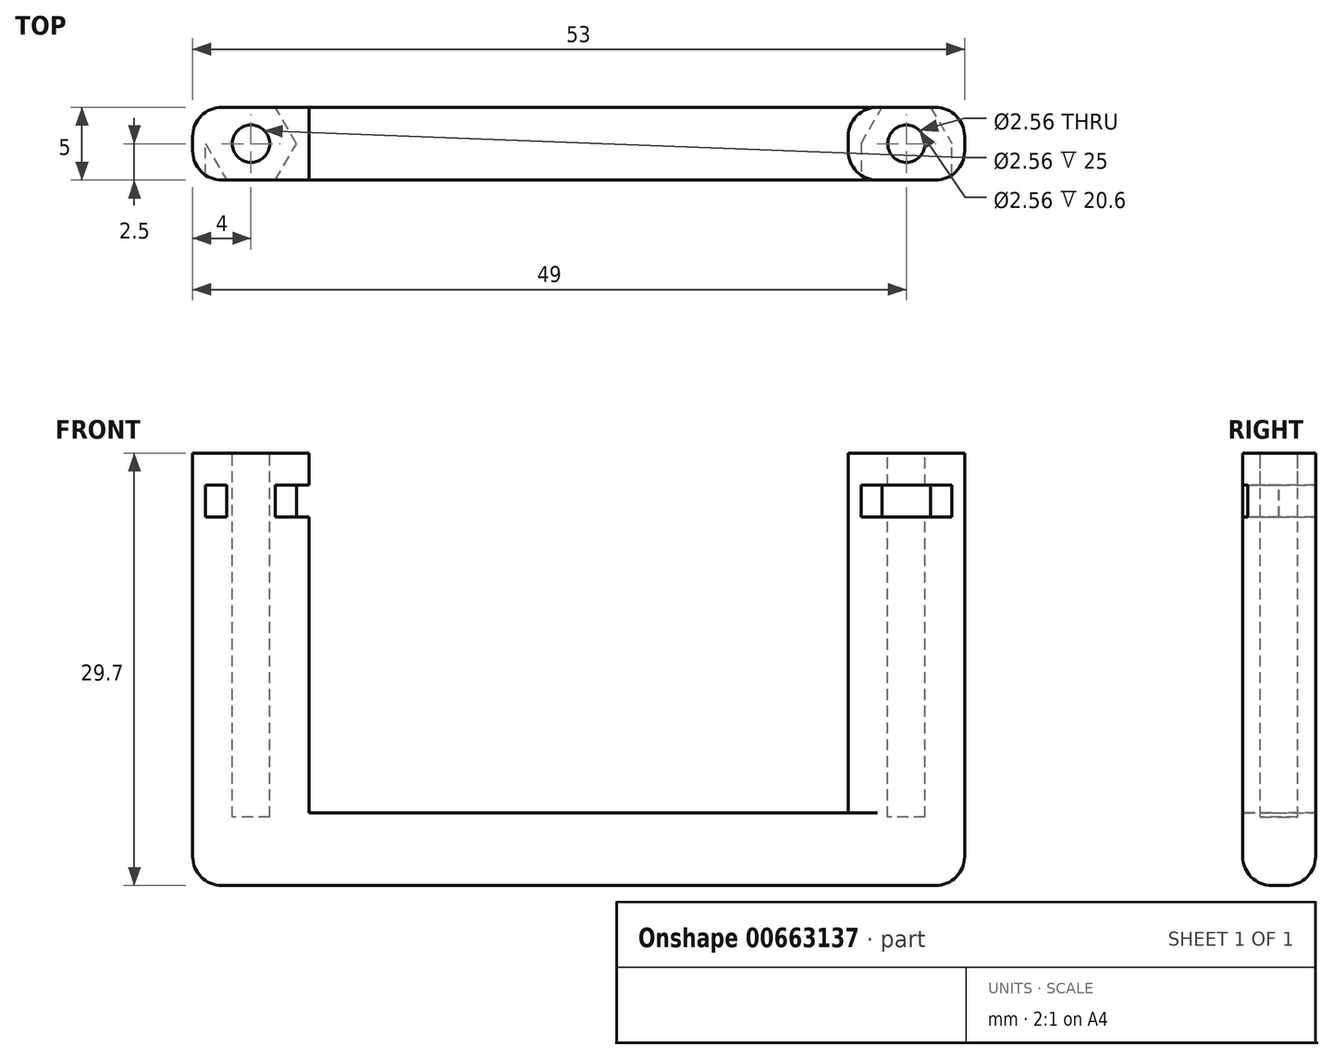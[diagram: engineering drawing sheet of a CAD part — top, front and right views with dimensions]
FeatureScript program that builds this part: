
annotation { "Feature Type Name" : "Feature", "Feature Type Description" : "" }
export const myFeature = defineFeature(function(context is Context, id is Id, definition is map)
    precondition{}
    {
        {
            var Q0;
            Q0=qCreatedBy(makeId("Front.planeOp"),FACE);
            var sketch = newSketch(context, id + "F0", { "sketchPlane" : qUnion([Q0])});
            skLineSegment(sketch, "E0", {"start": v(0, 0) * mm, "end": v(22.5, 0) * mm});
            skLineSegment(sketch, "E1", {"start": v(22.5, 0) * mm, "end": v(22.5, 22.5) * mm, "construction": true});
            skLineSegment(sketch, "E2", {"start": v(22.5, 0) * mm, "end": v(18.5, 0) * mm});
            skLineSegment(sketch, "E3", {"start": v(18.5, 0) * mm, "end": v(18.5, 22.5) * mm});
            skLineSegment(sketch, "E4", {"start": v(18.5, 22.5) * mm, "end": v(26.5, 22.5) * mm});
            skLineSegment(sketch, "E5", {"start": v(26.5, 22.5) * mm, "end": v(26.5, 0) * mm});
            skLineSegment(sketch, "E6", {"start": v(26.5, 0) * mm, "end": v(18.5, 0) * mm});
            skLineSegment(sketch, "E7", {"start": v(26.5, 0) * mm, "end": v(26.5, -5) * mm});
            skLineSegment(sketch, "E8", {"start": v(26.5, -5) * mm, "end": v(0, -5) * mm});
            skLineSegment(sketch, "E9", {"start": v(0, -5) * mm, "end": v(0, 0) * mm});
            skLineSegment(sketch, "E10", {"start": v(22.5, 24) * mm, "end": v(22.5, 22.5) * mm, "construction": true});
            skLineSegment(sketch, "E11", {"start": v(22.5, 22.5) * mm, "end": v(22.5, 20.5) * mm, "construction": true});
            skLineSegment(sketch, "E12", {"start": v(22.5, 20.5) * mm, "end": v(25.1, 20.5) * mm, "construction": true});
            skLineSegment(sketch, "E13", {"start": v(25.1, 20.5) * mm, "end": v(19.9, 20.5) * mm});
            skLineSegment(sketch, "E14", {"start": v(19.9, 20.5) * mm, "end": v(19.9, 22.5) * mm});
            skLineSegment(sketch, "E15", {"start": v(19.9, 22.5) * mm, "end": v(25.1, 22.5) * mm});
            skLineSegment(sketch, "E16", {"start": v(25.1, 22.5) * mm, "end": v(25.1, 20.5) * mm});
            skLineSegment(sketch, "E17", {"start": v(0, -11.25) * mm, "end": v(0, 30.63) * mm, "construction": true});
            skLineSegment(sketch, "E18.MirrorCS", {"start": v(-22.5, 24) * mm, "end": v(-22.5, 22.5) * mm, "construction": true});
            skLineSegment(sketch, "E19.MirrorCS", {"start": v(-22.5, 22.5) * mm, "end": v(-22.5, 20.5) * mm, "construction": true});
            skLineSegment(sketch, "E20.MirrorCS", {"start": v(-22.5, 0) * mm, "end": v(-18.5, 0) * mm});
            skLineSegment(sketch, "E21.MirrorCS", {"start": v(-19.9, 22.5) * mm, "end": v(-25.1, 22.5) * mm});
            skLineSegment(sketch, "E22.MirrorCS", {"start": v(-22.5, 0) * mm, "end": v(-22.5, 22.5) * mm, "construction": true});
            skLineSegment(sketch, "E23.MirrorCS", {"start": v(-22.5, 20.5) * mm, "end": v(-25.1, 20.5) * mm, "construction": true});
            skLineSegment(sketch, "E24.MirrorCS", {"start": v(-26.5, -5) * mm, "end": v(0, -5) * mm});
            skLineSegment(sketch, "E25.MirrorCS", {"start": v(-26.5, 0) * mm, "end": v(-26.5, -5) * mm});
            skLineSegment(sketch, "E26.MirrorCS", {"start": v(0, 0) * mm, "end": v(-22.5, 0) * mm});
            skLineSegment(sketch, "E27.MirrorCS", {"start": v(-18.5, 0) * mm, "end": v(-18.5, 22.5) * mm});
            skLineSegment(sketch, "E28.MirrorCS", {"start": v(-18.5, 22.5) * mm, "end": v(-26.5, 22.5) * mm});
            skLineSegment(sketch, "E29.MirrorCS", {"start": v(-26.5, 22.5) * mm, "end": v(-26.5, 0) * mm});
            skLineSegment(sketch, "E30.MirrorCS", {"start": v(-26.5, 0) * mm, "end": v(-18.5, 0) * mm});
            skLineSegment(sketch, "E31.MirrorCS", {"start": v(-19.9, 20.5) * mm, "end": v(-19.9, 22.5) * mm});
            skLineSegment(sketch, "E32.MirrorCS", {"start": v(-25.1, 22.5) * mm, "end": v(-25.1, 20.5) * mm});
            skLineSegment(sketch, "E33.MirrorCS", {"start": v(-25.1, 20.5) * mm, "end": v(-19.9, 20.5) * mm});
            skSolve(sketch);
        }
        {
            var Q0;
            {var subQ2=sQuery(id+"F0.wireOp",EDGE,"E0");Q0=makeQuery(id+"F0.imprint","IMPRINT",FACE,{"disambiguationData":[TD([[makeQuery(id+"F0.imprint","IMPRINT",EDGE,{"derivedFrom":subQ2}),-1.0]])]});}
            var Q1;
            {var subQ4=sQuery(id+"F0.wireOp",EDGE,"E3");Q1=makeQuery(id+"F0.imprint","IMPRINT",FACE,{"disambiguationData":[TD([[makeQuery(id+"F0.imprint","IMPRINT",EDGE,{"derivedFrom":subQ4}),-1.0]])]});}
            var Q2;
            Q2=makeQuery(id+"F0.imprint","IMPRINT",FACE,{"disambiguationData":[TD([[makeQuery(id+"F0.imprint","IMPRINT",EDGE,{"derivedFrom":sQuery(id+"F0.wireOp",EDGE,"E13")}),-1.0]])]});
            var Q3;
            Q3=makeQuery(id+"F0.imprint","IMPRINT",FACE,{"disambiguationData":[TD([[makeQuery(id+"F0.imprint","IMPRINT",EDGE,{"derivedFrom":sQuery(id+"F0.wireOp",EDGE,"E9")}),1.0]])]});
            var Q4;
            {var subQ3=sQuery(id+"F0.wireOp",EDGE,"E27.MirrorCS");Q4=makeQuery(id+"F0.imprint","IMPRINT",FACE,{"disambiguationData":[TD([[makeQuery(id+"F0.imprint","IMPRINT",EDGE,{"derivedFrom":subQ3}),1.0]])]});}
            var Q5;
            {var subQ0=sQuery(id+"F0.wireOp",EDGE,"E31.MirrorCS");Q5=makeQuery(id+"F0.imprint","IMPRINT",FACE,{"disambiguationData":[TD([[makeQuery(id+"F0.imprint","IMPRINT",EDGE,{"derivedFrom":subQ0}),1.0]])]});}
            extrude(context, id + "F1", {"entities" : qUnion([Q0, Q1, Q2, Q3, Q4, Q5]), "endBound" : BoundingType.SYMMETRIC, "depth" : 5 * mm, "offsetDistance" : 25 * mm});
        }
        {
            var Q0;
            {var subQ0=sQuery(id+"F0.wireOp",EDGE,"E4");Q0=makeQuery(id+"F1.opExtrude","SWEPT_FACE",FACE,{"disambiguationData":[OSD([subQ0]),TDD([makeQuery(id+"F0.imprint","IMPRINT",EDGE,{"disambiguationData":[TD([[makeQuery(id+"F0.imprint","INTERSECT",VERTEX,{"derivedFrom":[subQ0,sQuery(id+"F0.wireOp",EDGE,"E5")]}),1.0]])],"derivedFrom":subQ0})])]});}
            var sketch = newSketch(context, id + "F2", { "sketchPlane" : qUnion([Q0])});
            skPoint(sketch, "E34", {"position": v(18.5, 2.5) * mm});
            skPoint(sketch, "E35", {"position": v(18.5, -2.5) * mm});
            skLineSegment(sketch, "E36", {"start": v(26.5, -2.5) * mm, "end": v(18.5, -2.5) * mm});
            skLineSegment(sketch, "E37", {"start": v(18.5, 2.5) * mm, "end": v(26.5, 2.5) * mm});
            skLineSegment(sketch, "E38", {"start": v(26.5, 2.5) * mm, "end": v(26.5, -2.5) * mm});
            skLineSegment(sketch, "E39", {"start": v(18.5, -2.5) * mm, "end": v(18.5, 2.5) * mm});
            skLineSegment(sketch, "E40", {"start": v(18.5, 2.5) * mm, "end": v(22.5, 2.5) * mm, "construction": true});
            skLineSegment(sketch, "E41", {"start": v(22.5, 2.5) * mm, "end": v(22.5, 0) * mm, "construction": true});
            skCircle(sketch, "E42.cCircle", {"center": v(22.5, 0) * mm, "radius": 2.7 * mm, "construction": true});
            skLineSegment(sketch, "E42.0", {"start": v(24.05, 2.7) * mm, "end": v(25.62, 0.01) * mm});
            skLineSegment(sketch, "E42.1", {"start": v(25.62, 0.01) * mm, "end": v(24.07, -2.7) * mm});
            skLineSegment(sketch, "E42.2", {"start": v(24.07, -2.7) * mm, "end": v(20.95, -2.7) * mm});
            skLineSegment(sketch, "E42.3", {"start": v(20.95, -2.7) * mm, "end": v(19.38, -0.01) * mm});
            skLineSegment(sketch, "E42.4", {"start": v(19.38, -0.01) * mm, "end": v(20.93, 2.7) * mm});
            skLineSegment(sketch, "E42.5", {"start": v(20.93, 2.7) * mm, "end": v(24.05, 2.7) * mm});
            skPoint(sketch, "E42.0.midPoint", {"position": v(24.83, 1.36) * mm});
            skLineSegment(sketch, "E43", {"start": v(19.38, -0.01) * mm, "end": v(19.38, -2.5) * mm});
            skLineSegment(sketch, "E44", {"start": v(19.38, -2.5) * mm, "end": v(25.62, -2.5) * mm});
            skLineSegment(sketch, "E45", {"start": v(25.62, -2.5) * mm, "end": v(25.62, 0.01) * mm});
            skLineSegment(sketch, "E46.MirrorCS", {"start": v(-19.38, -2.5) * mm, "end": v(-25.62, -2.5) * mm});
            skLineSegment(sketch, "E47.MirrorCS", {"start": v(-20.95, -2.7) * mm, "end": v(-19.38, -0.01) * mm});
            skLineSegment(sketch, "E48.MirrorCS", {"start": v(-20.93, 2.7) * mm, "end": v(-24.05, 2.7) * mm});
            skLineSegment(sketch, "E49.MirrorCS", {"start": v(-24.07, -2.7) * mm, "end": v(-20.95, -2.7) * mm});
            skLineSegment(sketch, "E50.MirrorCS", {"start": v(-25.62, 0.01) * mm, "end": v(-24.07, -2.7) * mm});
            skLineSegment(sketch, "E51.MirrorCS", {"start": v(-24.05, 2.7) * mm, "end": v(-25.62, 0.01) * mm});
            skPoint(sketch, "E52.MirrorP", {"position": v(-18.5, -2.5) * mm});
            skLineSegment(sketch, "E53.MirrorCS", {"start": v(-18.5, 2.5) * mm, "end": v(-22.5, 2.5) * mm, "construction": true});
            skLineSegment(sketch, "E54.MirrorCS", {"start": v(-22.5, 2.5) * mm, "end": v(-22.5, 0) * mm, "construction": true});
            skPoint(sketch, "E55.MirrorP", {"position": v(-18.5, 2.5) * mm});
            skPoint(sketch, "E56.MirrorP", {"position": v(-24.83, 1.36) * mm});
            skLineSegment(sketch, "E57.MirrorCS", {"start": v(-19.38, -0.01) * mm, "end": v(-19.38, -2.5) * mm});
            skLineSegment(sketch, "E58.MirrorCS", {"start": v(-19.38, -0.01) * mm, "end": v(-20.93, 2.7) * mm});
            skLineSegment(sketch, "E59.MirrorCS", {"start": v(-18.5, -2.5) * mm, "end": v(-18.5, 2.5) * mm});
            skLineSegment(sketch, "E60.MirrorCS", {"start": v(-25.62, -2.5) * mm, "end": v(-25.62, 0.01) * mm});
            skLineSegment(sketch, "E61.MirrorCS", {"start": v(-26.5, -2.5) * mm, "end": v(-18.5, -2.5) * mm});
            skCircle(sketch, "E62.MirrorC", {"center": v(-22.5, 0) * mm, "radius": 2.7 * mm, "construction": true});
            skLineSegment(sketch, "E63.MirrorCS", {"start": v(-18.5, 2.5) * mm, "end": v(-26.5, 2.5) * mm});
            skLineSegment(sketch, "E64.MirrorCS", {"start": v(-26.5, 2.5) * mm, "end": v(-26.5, -2.5) * mm});
            skSolve(sketch);
        }
        {
            var Q0;
            {var subQ0=sQuery(id+"F2.wireOp",EDGE,"E43");Q0=makeQuery(id+"F2.imprint","IMPRINT",FACE,{"disambiguationData":[TD([[makeQuery(id+"F2.imprint","IMPRINT",EDGE,{"derivedFrom":subQ0}),1.0]])]});}
            var Q1;
            {var subQ1=sQuery(id+"F2.wireOp",EDGE,"E42.1");Q1=makeQuery(id+"F2.imprint","IMPRINT",FACE,{"disambiguationData":[TD([[makeQuery(id+"F2.imprint","IMPRINT",EDGE,{"derivedFrom":subQ1}),-1.0]])]});}
            var Q2;
            {var subQ0=sQuery(id+"F2.wireOp",EDGE,"E42.1");Q2=makeQuery(id+"F2.imprint","IMPRINT",FACE,{"disambiguationData":[TD([[makeQuery(id+"F2.imprint","IMPRINT",EDGE,{"derivedFrom":subQ0}),1.0]])]});}
            var Q3;
            {var subQ0=sQuery(id+"F2.wireOp",EDGE,"E50.MirrorCS");Q3=makeQuery(id+"F2.imprint","IMPRINT",FACE,{"disambiguationData":[TD([[makeQuery(id+"F2.imprint","IMPRINT",EDGE,{"derivedFrom":subQ0}),1.0]])]});}
            var Q4;
            {var subQ0=sQuery(id+"F2.wireOp",EDGE,"E50.MirrorCS");Q4=makeQuery(id+"F2.imprint","IMPRINT",FACE,{"disambiguationData":[TD([[makeQuery(id+"F2.imprint","IMPRINT",EDGE,{"derivedFrom":subQ0}),-1.0]])]});}
            var Q5;
            {var subQ0=sQuery(id+"F2.wireOp",EDGE,"E57.MirrorCS");Q5=makeQuery(id+"F2.imprint","IMPRINT",FACE,{"disambiguationData":[TD([[makeQuery(id+"F2.imprint","IMPRINT",EDGE,{"derivedFrom":subQ0}),-1.0]])]});}
            var Q6;
            {var subQ6=sQuery(id+"F2.wireOp",EDGE,"E47.MirrorCS");var subQ9=sQuery(id+"F2.wireOp",EDGE,"E61.MirrorCS");var subQ11=makeQuery(id+"F2.imprint","INTERSECT",VERTEX,{"derivedFrom":[subQ6,subQ9]});Q6=makeQuery(id+"F2.imprint","IMPRINT",FACE,{"disambiguationData":[TD([[makeQuery(id+"F2.imprint","IMPRINT",EDGE,{"disambiguationData":[TD([[subQ11,1.0]])],"derivedFrom":subQ9}),1.0]])]});}
            var Q7;
            {var subQ5=sQuery(id+"F2.wireOp",EDGE,"E42.4");var subQ9=sQuery(id+"F2.wireOp",EDGE,"E37");var subQ11=makeQuery(id+"F2.imprint","INTERSECT",VERTEX,{"derivedFrom":[subQ9,subQ5]});Q7=makeQuery(id+"F2.imprint","IMPRINT",FACE,{"disambiguationData":[TD([[makeQuery(id+"F2.imprint","IMPRINT",EDGE,{"disambiguationData":[TD([[subQ11,-1.0]])],"derivedFrom":subQ9}),-1.0]])]});}
            extrude(context, id + "F3", {"entities" : qUnion([Q0, Q1, Q2, Q3, Q4, Q5, Q6, Q7]), "operationType" : NewBodyOperationType.REMOVE, "oppositeDirection" : true, "depth" : 2.2 * mm, "offsetDistance" : 25 * mm});
        }
        {
            var Q0;
            {var subQ6=sQuery(id+"F0.wireOp",EDGE,"E15");var subQ10=sQuery(id+"F0.wireOp",EDGE,"E4");Q0=makeQuery(id+"F3.boolean.opBoolean","SPLIT",FACE,{"disambiguationData":[TD([makeQuery(id+"F3.opExtrude","SWEPT_FACE",FACE,{"disambiguationData":[OSD([sQuery(id+"F2.wireOp",EDGE,"E42.0")])]})])],"derivedFrom":makeQuery(id+"F1.opExtrude","SWEPT_FACE",FACE,{"disambiguationData":[OSD([subQ10,subQ6])]})});}
            var sketch = newSketch(context, id + "F4", { "sketchPlane" : qUnion([Q0])});
            skLineSegment(sketch, "E65", {"start": v(-26.5, 2.5) * mm, "end": v(-18.5, 2.5) * mm});
            skLineSegment(sketch, "E66", {"start": v(-18.5, 2.5) * mm, "end": v(-18.5, -2.5) * mm});
            skLineSegment(sketch, "E67", {"start": v(-18.5, -2.5) * mm, "end": v(-26.5, -2.5) * mm});
            skLineSegment(sketch, "E68", {"start": v(-26.5, -2.5) * mm, "end": v(-26.5, 2.5) * mm});
            skPoint(sketch, "E69", {"position": v(18.5, 2.5) * mm});
            skPoint(sketch, "E70", {"position": v(18.5, -2.5) * mm});
            skLineSegment(sketch, "E71", {"start": v(26.5, 2.5) * mm, "end": v(18.5, 2.5) * mm});
            skLineSegment(sketch, "E72", {"start": v(18.5, -2.5) * mm, "end": v(26.5, -2.5) * mm});
            skLineSegment(sketch, "E73", {"start": v(26.5, -2.5) * mm, "end": v(26.5, 2.5) * mm});
            skLineSegment(sketch, "E74", {"start": v(18.5, -2.5) * mm, "end": v(18.5, 2.5) * mm});
            skSolve(sketch);
        }
        {
            var Q0;
            Q0=makeQuery(id+"F4.imprint","IMPRINT",FACE,{"disambiguationData":[TD([[makeQuery(id+"F4.imprint","IMPRINT",EDGE,{"derivedFrom":sQuery(id+"F4.wireOp",EDGE,"E65")}),-1.0]])]});
            var Q1;
            {var subQ3=sQuery(id+"F4.wireOp",EDGE,"E74");Q1=makeQuery(id+"F4.imprint","IMPRINT",FACE,{"disambiguationData":[TD([[makeQuery(id+"F4.imprint","IMPRINT",EDGE,{"derivedFrom":subQ3}),-1.0]])]});}
            var Q2;
            {var subQ0=sQuery(id+"F4.wireOp",EDGE,"E73");Q2=makeQuery(id+"F4.imprint","IMPRINT",FACE,{"disambiguationData":[TD([[makeQuery(id+"F4.imprint","IMPRINT",EDGE,{"derivedFrom":subQ0}),1.0]])]});}
            extrude(context, id + "F5", {"entities" : qUnion([Q0, Q1, Q2]), "operationType" : NewBodyOperationType.ADD, "depth" : 2.2 * mm, "offsetDistance" : 25 * mm});
        }
        {
            var Q0;
            Q0=makeQuery(id+"F5.opExtrude","CAP_FACE",FACE,{"disambiguationData":[OSD([sQuery(id+"F4.wireOp",EDGE,"E71"),sQuery(id+"F4.wireOp",EDGE,"E72"),sQuery(id+"F4.wireOp",EDGE,"E73"),sQuery(id+"F4.wireOp",EDGE,"E74")])],"isStart":false});
            var sketch = newSketch(context, id + "F6", { "sketchPlane" : qUnion([Q0])});
            skLineSegment(sketch, "E75", {"start": v(-26.5, 2.5) * mm, "end": v(-22.5, 2.5) * mm, "construction": true});
            skLineSegment(sketch, "E76", {"start": v(-22.5, 2.5) * mm, "end": v(-22.5, 0) * mm, "construction": true});
            skLineSegment(sketch, "E77", {"start": v(18.5, 2.5) * mm, "end": v(22.5, 2.5) * mm, "construction": true});
            skLineSegment(sketch, "E78", {"start": v(22.5, 2.5) * mm, "end": v(22.5, 0) * mm, "construction": true});
            skCircle(sketch, "E79", {"center": v(22.5, 0) * mm, "radius": 1.28 * mm});
            skCircle(sketch, "E80", {"center": v(-22.5, 0) * mm, "radius": 1.28 * mm});
            skSolve(sketch);
        }
        {
            var Q0;
            Q0=makeQuery(id+"F6.imprint","IMPRINT",FACE,{"disambiguationData":[TD([[makeQuery(id+"F6.imprint","IMPRINT",EDGE,{"derivedFrom":sQuery(id+"F6.wireOp",EDGE,"E80")}),1.0]])]});
            var Q1;
            Q1=makeQuery(id+"F6.imprint","IMPRINT",FACE,{"disambiguationData":[TD([[makeQuery(id+"F6.imprint","IMPRINT",EDGE,{"derivedFrom":sQuery(id+"F6.wireOp",EDGE,"E79")}),1.0]])]});
            extrude(context, id + "F7", {"entities" : qUnion([Q0, Q1]), "operationType" : NewBodyOperationType.REMOVE, "oppositeDirection" : true, "depth" : 25 * mm, "offsetDistance" : 25 * mm});
        }
        {
            var Q0;
            Q0=makeQuery(id+"F1.opExtrude","SWEPT_FACE",FACE,{"disambiguationData":[OSD([sQuery(id+"F0.wireOp",EDGE,"E8"),sQuery(id+"F0.wireOp",EDGE,"E24.MirrorCS")])]});
            var Q1;
            Q1=makeQuery(id+"F5.boolean.opBoolean","MERGE",EDGE,{"derivedFrom":[makeQuery(id+"F1.opExtrude","CAP_EDGE",EDGE,{"disambiguationData":[OSD([sQuery(id+"F0.wireOp",EDGE,"E3")])],"isStart":false}),makeQuery(id+"F5.opExtrude","SWEPT_EDGE",EDGE,{"disambiguationData":[OSD([sQuery(id+"F4.wireOp",EDGE,"E72"),sQuery(id+"F4.wireOp",EDGE,"E74")])]})]});
            var Q2;
            Q2=makeQuery(id+"F5.boolean.opBoolean","MERGE",EDGE,{"derivedFrom":[makeQuery(id+"F1.opExtrude","CAP_EDGE",EDGE,{"disambiguationData":[OSD([sQuery(id+"F0.wireOp",EDGE,"E3")])],"isStart":true}),makeQuery(id+"F5.opExtrude","SWEPT_EDGE",EDGE,{"disambiguationData":[OSD([sQuery(id+"F4.wireOp",EDGE,"E71"),sQuery(id+"F4.wireOp",EDGE,"E74")])]})]});
            var Q3;
            Q3=makeQuery(id+"F5.boolean.opBoolean","MERGE",EDGE,{"derivedFrom":[makeQuery(id+"F1.opExtrude","CAP_EDGE",EDGE,{"disambiguationData":[OSD([sQuery(id+"F0.wireOp",EDGE,"E5"),sQuery(id+"F0.wireOp",EDGE,"E7")])],"isStart":false}),makeQuery(id+"F5.opExtrude","SWEPT_EDGE",EDGE,{"disambiguationData":[OSD([sQuery(id+"F4.wireOp",EDGE,"E72"),sQuery(id+"F4.wireOp",EDGE,"E73")])]})]});
            var Q4;
            Q4=makeQuery(id+"F1.opExtrude","CAP_EDGE",EDGE,{"disambiguationData":[OSD([sQuery(id+"F0.wireOp",EDGE,"E5"),sQuery(id+"F0.wireOp",EDGE,"E7")])],"isStart":true});
            var Q5;
            Q5=makeQuery(id+"F5.boolean.opBoolean","MERGE",EDGE,{"derivedFrom":[makeQuery(id+"F1.opExtrude","CAP_EDGE",EDGE,{"disambiguationData":[OSD([sQuery(id+"F0.wireOp",EDGE,"E25.MirrorCS"),sQuery(id+"F0.wireOp",EDGE,"E29.MirrorCS")])],"isStart":false}),makeQuery(id+"F5.opExtrude","SWEPT_EDGE",EDGE,{"disambiguationData":[OSD([sQuery(id+"F4.wireOp",EDGE,"E67"),sQuery(id+"F4.wireOp",EDGE,"E68")])]})]});
            var Q6;
            Q6=makeQuery(id+"F5.boolean.opBoolean","MERGE",EDGE,{"derivedFrom":[makeQuery(id+"F1.opExtrude","CAP_EDGE",EDGE,{"disambiguationData":[OSD([sQuery(id+"F0.wireOp",EDGE,"E25.MirrorCS"),sQuery(id+"F0.wireOp",EDGE,"E29.MirrorCS")])],"isStart":true}),makeQuery(id+"F5.opExtrude","SWEPT_EDGE",EDGE,{"disambiguationData":[OSD([sQuery(id+"F4.wireOp",EDGE,"E65"),sQuery(id+"F4.wireOp",EDGE,"E68")])]})]});
            var Q7;
            Q7=makeQuery(id+"F5.boolean.opBoolean","MERGE",EDGE,{"derivedFrom":[makeQuery(id+"F1.opExtrude","CAP_EDGE",EDGE,{"disambiguationData":[OSD([sQuery(id+"F0.wireOp",EDGE,"E27.MirrorCS")])],"isStart":false}),makeQuery(id+"F5.opExtrude","SWEPT_EDGE",EDGE,{"disambiguationData":[OSD([sQuery(id+"F4.wireOp",EDGE,"E66"),sQuery(id+"F4.wireOp",EDGE,"E67")])]})]});
            var Q8;
            Q8=makeQuery(id+"F5.boolean.opBoolean","MERGE",EDGE,{"derivedFrom":[makeQuery(id+"F1.opExtrude","CAP_EDGE",EDGE,{"disambiguationData":[OSD([sQuery(id+"F0.wireOp",EDGE,"E27.MirrorCS")])],"isStart":true}),makeQuery(id+"F5.opExtrude","SWEPT_EDGE",EDGE,{"disambiguationData":[OSD([sQuery(id+"F4.wireOp",EDGE,"E65"),sQuery(id+"F4.wireOp",EDGE,"E66")])]})]});
            fillet(context, id + "F8", {"entities" : qUnion([Q0, Q1, Q2, Q3, Q4, Q5, Q6, Q7, Q8]), "radius" : 2 * mm, "tangentPropagation" : true, "allowEdgeOverflow" : false});
        }
    });
